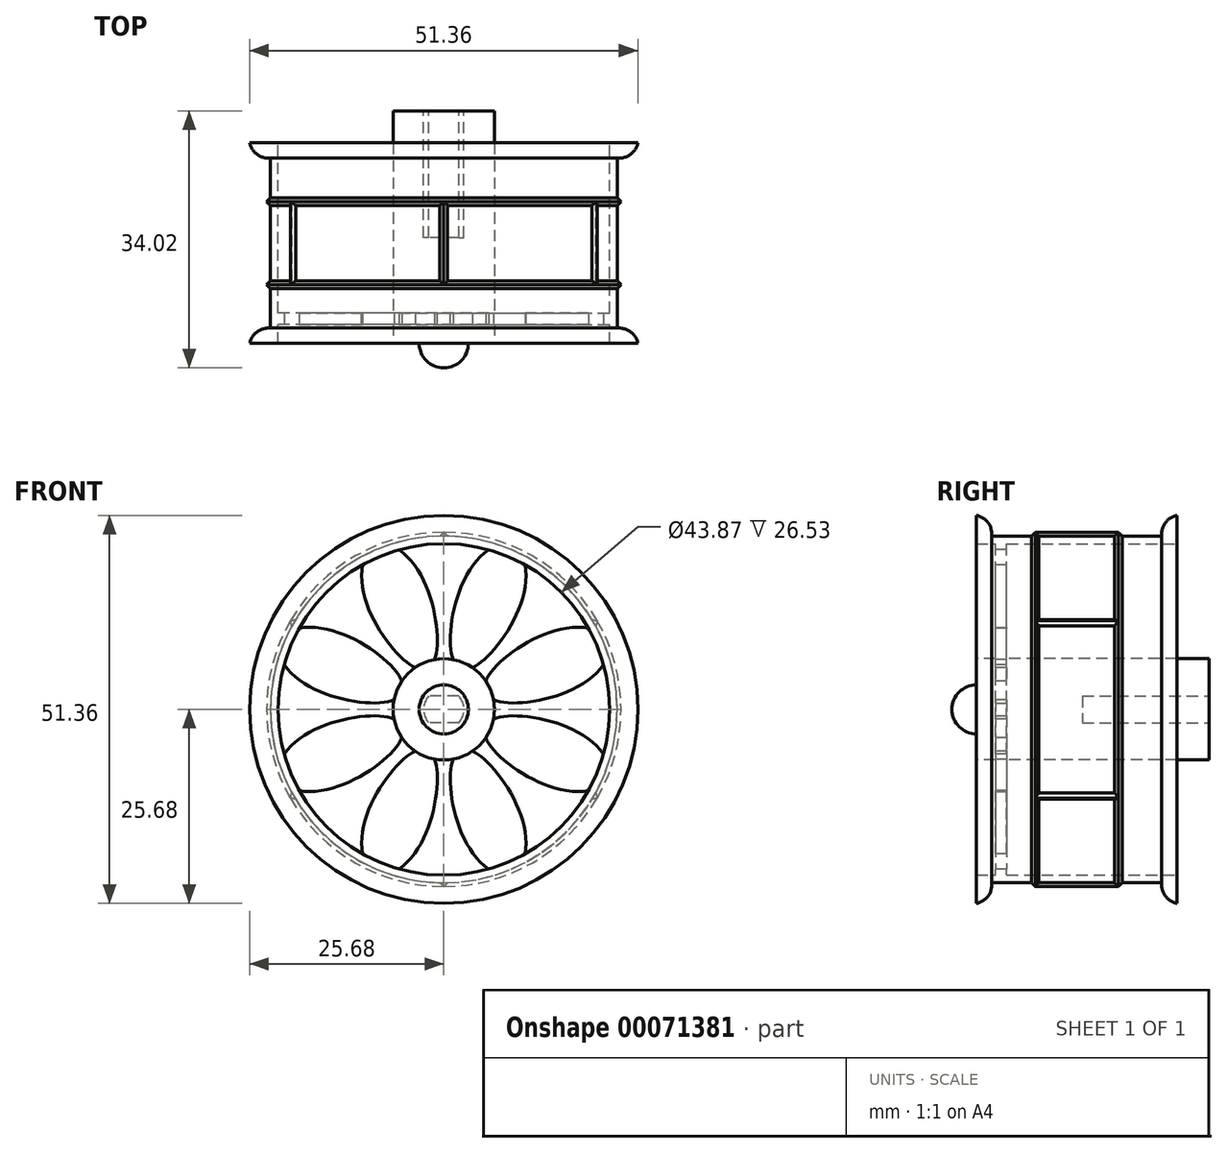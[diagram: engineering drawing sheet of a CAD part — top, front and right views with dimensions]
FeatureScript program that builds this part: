
annotation { "Feature Type Name" : "Feature", "Feature Type Description" : "" }
export const myFeature = defineFeature(function(context is Context, id is Id, definition is map)
    precondition{}
    {
        {
            var Q0;
            Q0=qCreatedBy(makeId("Front.planeOp"),FACE);
            var sketch = newSketch(context, id + "F0", { "sketchPlane" : qUnion([Q0])});
            skCircle(sketch, "E0", {"center": v(0, 0) * mm, "radius": 22.94 * mm});
            skCircle(sketch, "E1", {"center": v(0, 0) * mm, "radius": 21.93 * mm});
            skCircle(sketch, "E2", {"center": v(0, 0) * mm, "radius": 6.7 * mm});
            skSolve(sketch);
        }
        {
            var Q0;
            Q0=makeQuery(id+"F0.imprint","IMPRINT",FACE,{"disambiguationData":[TD([[makeQuery(id+"F0.imprint","IMPRINT",EDGE,{"derivedFrom":sQuery(id+"F0.wireOp",EDGE,"E0")}),1.0]])]});
            extrude(context, id + "F1", {"entities" : qUnion([Q0]), "depth" : 26.53 * mm, "symmetric" : true});
        }
        {
            var Q0;
            Q0=makeQuery(id+"F0.imprint","IMPRINT",FACE,{"disambiguationData":[TD([[makeQuery(id+"F0.imprint","IMPRINT",EDGE,{"derivedFrom":sQuery(id+"F0.wireOp",EDGE,"E2")}),1.0]])]});
            extrude(context, id + "F2", {"entities" : qUnion([Q0]), "oppositeDirection" : true, "depth" : 17.5 * mm});
        }
        {
            var Q0;
            Q0=makeQuery(id+"F0.imprint","IMPRINT",FACE,{"disambiguationData":[TD([[makeQuery(id+"F0.imprint","IMPRINT",EDGE,{"derivedFrom":sQuery(id+"F0.wireOp",EDGE,"E2")}),1.0]])]});
            extrude(context, id + "F3", {"entities" : qUnion([Q0]), "operationType" : NewBodyOperationType.ADD, "depth" : (26.53 / 2) * mm});
        }
        {
            var Q0;
            Q0=makeQuery(id+"F2.opExtrude","CAP_FACE",FACE,{"disambiguationData":[OSD([sQuery(id+"F0.wireOp",EDGE,"E2")])],"isStart":false});
            var sketch = newSketch(context, id + "F4", { "sketchPlane" : qUnion([Q0])});
            skCircle(sketch, "E3", {"center": v(0, 0) * mm, "radius": 2.67 * mm});
            skLineSegment(sketch, "E4", {"start": v(-1.98, -1.78) * mm, "end": v(1.98, -1.78) * mm});
            skLineSegment(sketch, "E5", {"start": v(-1.98, 1.78) * mm, "end": v(1.98, 1.78) * mm});
            skSolve(sketch);
        }
        {
            var Q0;
            {var subQ0=sQuery(id+"F4.wireOp",EDGE,"E4");Q0=makeQuery(id+"F4.imprint","IMPRINT",FACE,{"disambiguationData":[TD([[makeQuery(id+"F4.imprint","IMPRINT",EDGE,{"derivedFrom":subQ0}),1.0]])]});}
            extrude(context, id + "F5", {"entities" : qUnion([Q0]), "operationType" : NewBodyOperationType.REMOVE, "oppositeDirection" : true, "depth" : 16.75 * mm});
        }
        {
            var Q0;
            Q0=makeQuery(id+"F1.opExtrude","CAP_FACE",FACE,{"disambiguationData":[OSD([sQuery(id+"F0.wireOp",EDGE,"E0"),sQuery(id+"F0.wireOp",EDGE,"E1")])],"isStart":true});
            var sketch = newSketch(context, id + "F6", { "sketchPlane" : qUnion([Q0])});
            skCircle(sketch, "E6", {"center": v(0, 0) * mm, "radius": 25.68 * mm});
            skCircle(sketch, "E7", {"center": v(0, 0) * mm, "radius": 22.94 * mm});
            skSolve(sketch);
        }
        {
            var Q0;
            Q0 = qSketchRegion(id + "F6", true);
            extrude(context, id + "F7", {"entities" : qUnion([Q0]), "oppositeDirection" : true, "depth" : 2.02 * mm});
        }
        {
            var Q0;
            Q0=makeQuery(id+"F3.opExtrude","CAP_FACE",FACE,{"disambiguationData":[OSD([sQuery(id+"F0.wireOp",EDGE,"E2")])],"isStart":false});
            var sketch = newSketch(context, id + "F8", { "sketchPlane" : qUnion([Q0])});
            skCircle(sketch, "E8", {"center": v(0, 0) * mm, "radius": 3.25 * mm});
            skLineSegment(sketch, "E9", {"start": v(0, 0) * mm, "end": v(0, 3.25) * mm});
            skLineSegment(sketch, "E10", {"start": v(0, 0) * mm, "end": v(0, -3.25) * mm});
            skSolve(sketch);
        }
        {
            var Q0;
            {var subQ0=sQuery(id+"F8.wireOp",EDGE,"E9");Q0=makeQuery(id+"F8.imprint","IMPRINT",FACE,{"disambiguationData":[TD([[makeQuery(id+"F8.imprint","IMPRINT",EDGE,{"derivedFrom":subQ0}),-1.0]])]});}
            var Q1;
            Q1=sQuery(id+"F8.wireOp",EDGE,"E9");
            revolve(context, id + "F9", {"operationType" : NewBodyOperationType.ADD, "entities" : qUnion([Q0]), "axis" : qUnion([Q1]), "revolveType" : RevolveType.FULL});
        }
        {
            var Q0;
            Q0=qCreatedBy(makeId("Front.planeOp"),FACE);
            cPlane(context, id + "F10", {"entities" : qUnion([Q0]), "cplaneType" : CPlaneType.OFFSET, "offset" : 10 * mm, "width" : 150 * mm, "height" : 150 * mm});
        }
        {
            var Q0;
            Q0=qCreatedBy(id+"F10.planeOp",FACE);
            var sketch = newSketch(context, id + "F11", { "sketchPlane" : qUnion([Q0])});
            skLineSegment(sketch, "E11", {"start": v(0, 6.7) * mm, "end": v(0, 22.34) * mm});
            skFitSpline(sketch, "E12", {"points": [v(-1.25, 6.58) * mm, v(-7.04, 21.71) * mm], "startDerivative": vector(3.75, 8.67) * mm, "endDerivative": vector(-16.2, 6.61) * mm});
            skLineSegment(sketch, "E13", {"start": v(-7.04, 21.71) * mm, "end": v(0, 22.34) * mm});
            skLineSegment(sketch, "E14", {"start": v(-1.25, 6.58) * mm, "end": v(0, 6.7) * mm});
            skSolve(sketch);
        }
        {
            var Q0;
            {var subQ0=sQuery(id+"F11.wireOp",EDGE,"E11");Q0=makeQuery(id+"F11.imprint","IMPRINT",FACE,{"disambiguationData":[TD([[makeQuery(id+"F11.imprint","IMPRINT",EDGE,{"derivedFrom":subQ0}),1.0]])]});}
            extrude(context, id + "F12", {"entities" : qUnion([Q0]), "oppositeDirection" : true, "depth" : 1.5 * mm, "symmetric" : true});
        }
        {
            var Q0;
            Q0=makeQuery(id+"F12.split0.splitOp","SPLIT",BODY,{"derivedFrom":makeQuery(id+"F12.opExtrude","SWEPT_BODY",BODY,{"disambiguationData":[OSD([sQuery(id+"F0.wireOp",EDGE,"E2"),sQuery(id+"F11.wireOp",EDGE,"E11"),sQuery(id+"F11.wireOp",EDGE,"E12"),sQuery(id+"F11.wireOp",EDGE,"E13")])]})});
            var Q1;
            Q1=qCreatedBy(makeId("Right.planeOp"),FACE);
            mirror(context, id + "F13", {"entities" : qUnion([Q0]), "mirrorPlane" : qUnion([Q1])});
        }
        {
            var Q0;
            Q0=makeQuery(id+"F13.opPattern","COPY",BODY,{"derivedFrom":makeQuery(id+"F12.split0.splitOp","SPLIT",BODY,{"derivedFrom":makeQuery(id+"F12.opExtrude","SWEPT_BODY",BODY,{"disambiguationData":[OSD([sQuery(id+"F0.wireOp",EDGE,"E2"),sQuery(id+"F11.wireOp",EDGE,"E11"),sQuery(id+"F11.wireOp",EDGE,"E12"),sQuery(id+"F11.wireOp",EDGE,"E13")])]})}),"instanceName":"1"});
            var Q1;
            Q1=makeQuery(id+"F12.split0.splitOp","SPLIT",BODY,{"derivedFrom":makeQuery(id+"F12.opExtrude","SWEPT_BODY",BODY,{"disambiguationData":[OSD([sQuery(id+"F0.wireOp",EDGE,"E2"),sQuery(id+"F11.wireOp",EDGE,"E11"),sQuery(id+"F11.wireOp",EDGE,"E12"),sQuery(id+"F11.wireOp",EDGE,"E13")])]})});
            var Q2;
            Q2=makeQuery(id+"F12.opExtrude","CAP_FACE",FACE,{"disambiguationData":[OSD([sQuery(id+"F11.wireOp",EDGE,"E11"),sQuery(id+"F11.wireOp",EDGE,"E12"),sQuery(id+"F11.wireOp",EDGE,"E13"),sQuery(id+"F11.wireOp",EDGE,"E14")])],"isStart":true});
            var Q3;
            Q3=makeQuery(id+"F13.opPattern","COPY",FACE,{"derivedFrom":makeQuery(id+"F12.opExtrude","CAP_FACE",FACE,{"disambiguationData":[OSD([sQuery(id+"F11.wireOp",EDGE,"E11"),sQuery(id+"F11.wireOp",EDGE,"E12"),sQuery(id+"F11.wireOp",EDGE,"E13"),sQuery(id+"F11.wireOp",EDGE,"E14")])],"isStart":true}),"instanceName":"1"});
            var Q4;
            Q4=makeQuery(id+"F13.opPattern","COPY",FACE,{"derivedFrom":makeQuery(id+"F12.opExtrude","SWEPT_FACE",FACE,{"disambiguationData":[OSD([sQuery(id+"F11.wireOp",EDGE,"E12")])]}),"instanceName":"1"});
            var Q5;
            Q5=makeQuery(id+"F12.opExtrude","SWEPT_FACE",FACE,{"disambiguationData":[OSD([sQuery(id+"F11.wireOp",EDGE,"E12")])]});
            var Q6;
            Q6=makeQuery(id+"F12.opExtrude","CAP_FACE",FACE,{"disambiguationData":[OSD([sQuery(id+"F11.wireOp",EDGE,"E11"),sQuery(id+"F11.wireOp",EDGE,"E12"),sQuery(id+"F11.wireOp",EDGE,"E13"),sQuery(id+"F11.wireOp",EDGE,"E14")])],"isStart":false});
            var Q7;
            Q7=makeQuery(id+"F13.opPattern","COPY",FACE,{"derivedFrom":makeQuery(id+"F12.opExtrude","CAP_FACE",FACE,{"disambiguationData":[OSD([sQuery(id+"F11.wireOp",EDGE,"E11"),sQuery(id+"F11.wireOp",EDGE,"E12"),sQuery(id+"F11.wireOp",EDGE,"E13"),sQuery(id+"F11.wireOp",EDGE,"E14")])],"isStart":false}),"instanceName":"1"});
            var Q8;
            Q8=sQuery(id+"F0.wireOp",EDGE,"E2");
            circularPattern(context, id + "F14", {"operationType" : NewBodyOperationType.ADD, "entities" : qUnion([Q0, Q1]), "axis" : qUnion([Q8]), "angle" : 360 * degree, "instanceCount" : 8, "equalSpace" : true});
        }
        {
            var Q0;
            Q0=makeQuery(id+"F7.opExtrude","SWEPT_BODY",BODY,{"disambiguationData":[OSD([sQuery(id+"F6.wireOp",EDGE,"E6"),sQuery(id+"F6.wireOp",EDGE,"E7")])]});
            var Q1;
            Q1=qCreatedBy(makeId("Front.planeOp"),FACE);
            mirror(context, id + "F15", {"operationType" : NewBodyOperationType.ADD, "entities" : qUnion([Q0]), "mirrorPlane" : qUnion([Q1])});
        }
        {
            var Q0;
            Q0=qCreatedBy(makeId("Front.planeOp"),FACE);
            cPlane(context, id + "F16", {"entities" : qUnion([Q0]), "cplaneType" : CPlaneType.OFFSET, "offset" : 5.5 * mm, "width" : 150 * mm, "height" : 150 * mm});
        }
        {
            var Q0;
            Q0=qCreatedBy(id+"F16.planeOp",FACE);
            var sketch = newSketch(context, id + "F17", { "sketchPlane" : qUnion([Q0])});
            skCircle(sketch, "E15", {"center": v(0, 0) * mm, "radius": 22.94 * mm});
            skCircle(sketch, "E16", {"center": v(0, 0) * mm, "radius": 23.44 * mm});
            skSolve(sketch);
        }
        {
            var Q0;
            Q0 = qSketchRegion(id + "F17", true);
            extrude(context, id + "F18", {"entities" : qUnion([Q0]), "operationType" : NewBodyOperationType.ADD, "depth" : 1 * mm, "symmetric" : true});
        }
        {
            var Q0;
            Q0=makeQuery(id+"F18.opExtrude","CAP_EDGE",EDGE,{"disambiguationData":[OSD([sQuery(id+"F17.wireOp",EDGE,"E16")])],"isStart":false});
            var Q1;
            Q1=makeQuery(id+"F18.opExtrude","CAP_EDGE",EDGE,{"disambiguationData":[OSD([sQuery(id+"F17.wireOp",EDGE,"E16")])],"isStart":true});
            chamfer(context, id + "F19", {"entities" : qUnion([Q0, Q1]), "width" : .5 * mm, "tangentPropagation" : true});
        }
        {
            var Q0;
            {var subQ0=sQuery(id+"F17.wireOp",EDGE,"E16");Q0=makeQuery(id+"F19.opChamfer","BLEND_FACE",FACE,{"disambiguationData":[OSD([subQ0]),TDD([makeQuery(id+"F18.opExtrude","CAP_EDGE",EDGE,{"disambiguationData":[OSD([subQ0])],"isStart":false})])]});}
            var Q1;
            {var subQ0=sQuery(id+"F17.wireOp",EDGE,"E16");Q1=makeQuery(id+"F19.opChamfer","BLEND_FACE",FACE,{"disambiguationData":[OSD([subQ0]),TDD([makeQuery(id+"F18.opExtrude","CAP_EDGE",EDGE,{"disambiguationData":[OSD([subQ0])],"isStart":true})])]});}
            var Q2;
            Q2=qCreatedBy(makeId("Front.planeOp"),FACE);
            mirror(context, id + "F20", {"faces" : qUnion([Q0, Q1]), "mirrorPlane" : qUnion([Q2]), "patternType" : MirrorType.FACE});
        }
        {
            var Q0;
            Q0=qCreatedBy(makeId("Top.planeOp"),FACE);
            cPlane(context, id + "F21", {"entities" : qUnion([Q0]), "cplaneType" : CPlaneType.OFFSET, "offset" : 22.94 * mm, "width" : 150 * mm, "height" : 150 * mm});
        }
        {
            var Q0;
            Q0=qCreatedBy(id+"F21.planeOp",FACE);
            var sketch = newSketch(context, id + "F22", { "sketchPlane" : qUnion([Q0])});
            skLineSegment(sketch, "E17.bottom", {"start": v(0.5, -5.5) * mm, "end": v(-0.5, -5.5) * mm});
            skLineSegment(sketch, "E17.top", {"start": v(0.5, 5.5) * mm, "end": v(-0.5, 5.5) * mm});
            skLineSegment(sketch, "E17.left", {"start": v(0.5, -5.5) * mm, "end": v(0.5, 5.5) * mm});
            skLineSegment(sketch, "E17.right", {"start": v(-0.5, -5.5) * mm, "end": v(-0.5, 5.5) * mm});
            skPoint(sketch, "E17.middle", {"position": v(0, 0) * mm});
            skSolve(sketch);
        }
        {
            var Q0;
            Q0 = qSketchRegion(id + "F22", true);
            extrude(context, id + "F23", {"entities" : qUnion([Q0]), "depth" : .5 * mm});
        }
        {
            var Q0;
            Q0=makeQuery(id+"F23.opExtrude","CAP_EDGE",EDGE,{"disambiguationData":[OSD([sQuery(id+"F22.wireOp",EDGE,"E17.left")])],"isStart":false});
            var Q1;
            Q1=makeQuery(id+"F23.opExtrude","CAP_EDGE",EDGE,{"disambiguationData":[OSD([sQuery(id+"F22.wireOp",EDGE,"E17.right")])],"isStart":false});
            chamfer(context, id + "F24", {"entities" : qUnion([Q0, Q1]), "width" : .5 * mm, "tangentPropagation" : true});
        }
        {
            var Q0;
            Q0=makeQuery(id+"F23.opExtrude","SWEPT_BODY",BODY,{"disambiguationData":[OSD([sQuery(id+"F22.wireOp",EDGE,"E17.bottom"),sQuery(id+"F22.wireOp",EDGE,"E17.top"),sQuery(id+"F22.wireOp",EDGE,"E17.left"),sQuery(id+"F22.wireOp",EDGE,"E17.right")])]});
            var Q1;
            Q1=makeQuery(id+"F3.opExtrude","CAP_EDGE",EDGE,{"disambiguationData":[OSD([sQuery(id+"F0.wireOp",EDGE,"E2")])],"isStart":false});
            circularPattern(context, id + "F25", {"operationType" : NewBodyOperationType.ADD, "entities" : qUnion([Q0]), "axis" : qUnion([Q1]), "angle" : 360 * degree, "instanceCount" : 6, "equalSpace" : true});
        }
        {
            var Q0;
            Q0=makeQuery(id+"F15.opPattern","COPY",EDGE,{"derivedFrom":makeQuery(id+"F7.opExtrude","CAP_EDGE",EDGE,{"disambiguationData":[OSD([sQuery(id+"F6.wireOp",EDGE,"E6")])],"isStart":false}),"instanceName":"1"});
            var Q1;
            Q1=makeQuery(id+"F7.opExtrude","CAP_EDGE",EDGE,{"disambiguationData":[OSD([sQuery(id+"F6.wireOp",EDGE,"E6")])],"isStart":false});
            fillet(context, id + "F26", {"entities" : qUnion([Q0, Q1]), "radius" : 2.5 * mm, "tangentPropagation" : true, "allowEdgeOverflow" : false});
        }
    });
